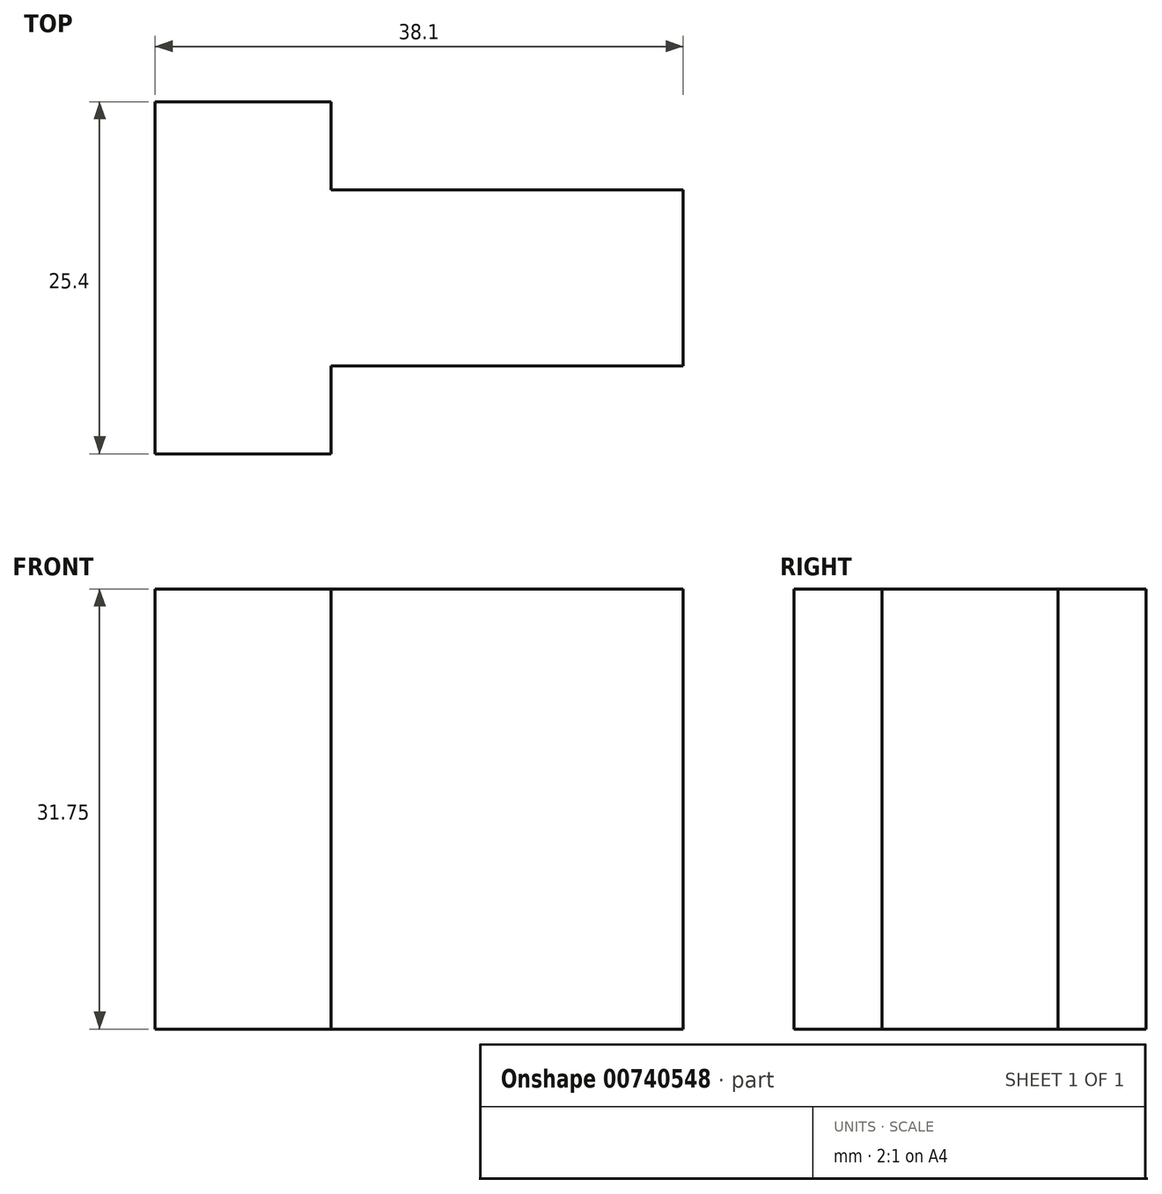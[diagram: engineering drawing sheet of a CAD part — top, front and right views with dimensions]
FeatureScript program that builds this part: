
annotation { "Feature Type Name" : "Feature", "Feature Type Description" : "" }
export const myFeature = defineFeature(function(context is Context, id is Id, definition is map)
    precondition{}
    {
        {
            var Q0;
            Q0=qCreatedBy(makeId("Top.planeOp"),FACE);
            var sketch = newSketch(context, id + "F0", { "sketchPlane" : qUnion([Q0])});
            skLineSegment(sketch, "E0", {"start": v(0, 25.4) * mm, "end": v(0, 0) * mm});
            skLineSegment(sketch, "E1", {"start": v(0, 0) * mm, "end": v(12.7, 0) * mm});
            skLineSegment(sketch, "E2", {"start": v(12.7, 0) * mm, "end": v(12.7, 6.35) * mm});
            skLineSegment(sketch, "E3", {"start": v(12.7, 6.35) * mm, "end": v(38.1, 6.35) * mm});
            skLineSegment(sketch, "E4", {"start": v(38.1, 6.35) * mm, "end": v(38.1, 19.05) * mm});
            skLineSegment(sketch, "E5", {"start": v(38.1, 19.05) * mm, "end": v(12.7, 19.05) * mm});
            skLineSegment(sketch, "E6", {"start": v(12.7, 19.05) * mm, "end": v(12.7, 25.4) * mm});
            skLineSegment(sketch, "E7", {"start": v(12.7, 25.4) * mm, "end": v(0, 25.4) * mm});
            skSolve(sketch);
        }
        {
            var Q0;
            Q0 = qSketchRegion(id + "F0", true);
            extrude(context, id + "F1", {"entities" : qUnion([Q0]), "depth" : 31.75 * mm, "offsetDistance" : 25.4 * mm});
        }
    });
